# Revit family: QF_BOURGEAT_Gamme_standard_Avec_plan_de_travail
name_source: partatom
category: Equipement spécialisé
revit_build: Autodesk Revit 2015 (Build: 20140606_1530(x64)
units: mm (PartAtom-declared; Revit-internal decimal feet)

## types (3) — shared parameters
Charge max = 200.00 kg
Charge maximale = 20 kg par glissière; 200kg par chariot
Fabricant = BOURGEAT
Hauteur echelle = 736 mm
Hauteur hors tout = 900 mm  [stored 2.95276 ft]
Niveaux = 7
Spécification du Fabricant = Charrot à glissières bas avec plan de travail
URL catalogue = http://www.bourgeat.fr

## per-type parameters (varying)
| type | Barre renfort | Entrée | Longueur hors tout | Modèle | Poids net à vide | Profondeur echelle | Profondeur hors tout |
| GN1/1-7 niveaux - Espacement 89 mm | 335 mm  [stored 1.09908 ft] | 325 mm  [stored 1.06627 ft] | 460 mm  [stored 1.50919 ft] | 771506 | 13.00 kg | 555 mm  [stored 1.82087 ft] | 630 mm  [stored 2.06693 ft] |
| GN2/1-7 niveaux - Espacement 89 mm | 535 mm | 530 mm  [stored 1.73885 ft] | 660 mm | 771006 | 16.50 kg | 625 mm  [stored 2.05052 ft] | 700 mm  [stored 2.29659 ft] |
| "Pâtissier" 600x400-7 niveaux - Espacement 89 mm | 405 mm  [stored 1.32874 ft] | 400 mm  [stored 1.31234 ft] | 530 mm  [stored 1.73885 ft] | 770506 | 16.00 kg | 625 mm  [stored 2.05052 ft] | 700 mm  [stored 2.29659 ft] |

note: [stored X ft] marks values corroborated as IEEE doubles in the binary element streams (Revit-internal decimal feet)
